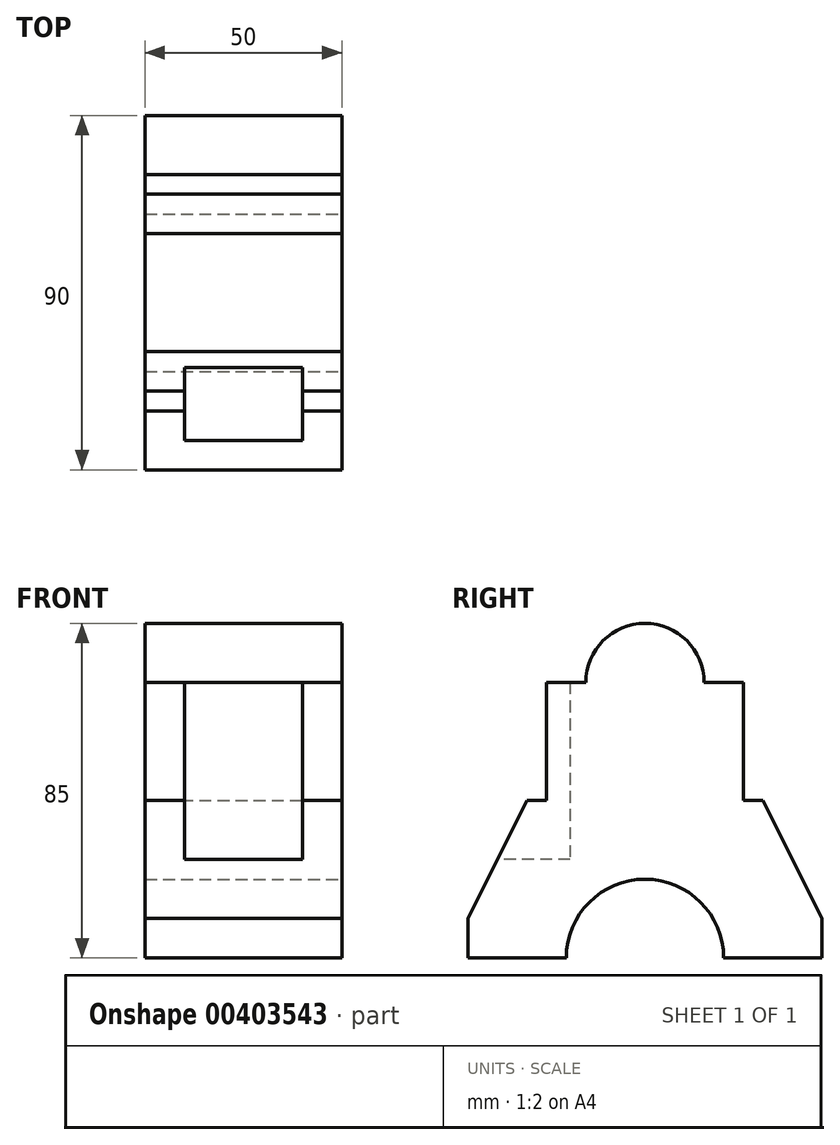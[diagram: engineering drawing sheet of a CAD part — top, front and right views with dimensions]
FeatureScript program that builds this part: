
annotation { "Feature Type Name" : "Feature", "Feature Type Description" : "" }
export const myFeature = defineFeature(function(context is Context, id is Id, definition is map)
    precondition{}
    {
        {
            var Q0;
            Q0=qCreatedBy(makeId("Right.planeOp"),FACE);
            var sketch = newSketch(context, id + "F0", { "sketchPlane" : qUnion([Q0])});
            skLineSegment(sketch, "E0", {"start": v(0, 0) * mm, "end": v(45, 0) * mm});
            skLineSegment(sketch, "E1", {"start": v(45, 0) * mm, "end": v(45, 10) * mm});
            skLineSegment(sketch, "E2", {"start": v(45, 10) * mm, "end": v(30, 40) * mm});
            skLineSegment(sketch, "E3", {"start": v(30, 40) * mm, "end": v(25, 40) * mm});
            skLineSegment(sketch, "E4", {"start": v(25, 40) * mm, "end": v(25, 70) * mm});
            skLineSegment(sketch, "E5", {"start": v(25, 70) * mm, "end": v(0, 70) * mm});
            skLineSegment(sketch, "E6", {"start": v(0, 70) * mm, "end": v(0, 0) * mm, "construction": true});
            skLineSegment(sketch, "E7.MirrorCS", {"start": v(-30, 40) * mm, "end": v(-25, 40) * mm});
            skLineSegment(sketch, "E8.MirrorCS", {"start": v(-25, 40) * mm, "end": v(-25, 70) * mm});
            skLineSegment(sketch, "E9.MirrorCS", {"start": v(0, 0) * mm, "end": v(-45, 0) * mm});
            skLineSegment(sketch, "E10.MirrorCS", {"start": v(-25, 70) * mm, "end": v(0, 70) * mm});
            skLineSegment(sketch, "E11.MirrorCS", {"start": v(-45, 10) * mm, "end": v(-30, 40) * mm});
            skLineSegment(sketch, "E12.MirrorCS", {"start": v(-45, 0) * mm, "end": v(-45, 10) * mm});
            skSolve(sketch);
        }
        {
            var Q0;
            Q0 = qSketchRegion(id + "F0", true);
            extrude(context, id + "F1", {"entities" : qUnion([Q0]), "endBound" : BoundingType.SYMMETRIC, "oppositeDirection" : true, "depth" : 50 * mm});
        }
        {
            var Q0;
            Q0=makeQuery(id+"F1.opExtrude","CAP_FACE",FACE,{"disambiguationData":[OSD([sQuery(id+"F0.wireOp",EDGE,"E0"),sQuery(id+"F0.wireOp",EDGE,"E1"),sQuery(id+"F0.wireOp",EDGE,"E2"),sQuery(id+"F0.wireOp",EDGE,"E3"),sQuery(id+"F0.wireOp",EDGE,"E4"),sQuery(id+"F0.wireOp",EDGE,"E5"),sQuery(id+"F0.wireOp",EDGE,"E7.MirrorCS"),sQuery(id+"F0.wireOp",EDGE,"E8.MirrorCS"),sQuery(id+"F0.wireOp",EDGE,"E9.MirrorCS"),sQuery(id+"F0.wireOp",EDGE,"E10.MirrorCS"),sQuery(id+"F0.wireOp",EDGE,"E11.MirrorCS"),sQuery(id+"F0.wireOp",EDGE,"E12.MirrorCS")])],"isStart":true});
            var sketch = newSketch(context, id + "F2", { "sketchPlane" : qUnion([Q0])});
            skCircle(sketch, "E13", {"center": v(0, 0) * mm, "radius": 20 * mm});
            skSolve(sketch);
        }
        {
            var Q0;
            Q0 = qSketchRegion(id + "F2", true);
            extrude(context, id + "F3", {"entities" : qUnion([Q0]), "operationType" : NewBodyOperationType.REMOVE, "endBound" : BoundingType.THROUGH_ALL, "oppositeDirection" : true, "depth" : 25 * mm});
        }
        {
            var Q0;
            Q0=makeQuery(id+"F1.opExtrude","CAP_FACE",FACE,{"disambiguationData":[OSD([sQuery(id+"F0.wireOp",EDGE,"E0"),sQuery(id+"F0.wireOp",EDGE,"E1"),sQuery(id+"F0.wireOp",EDGE,"E2"),sQuery(id+"F0.wireOp",EDGE,"E3"),sQuery(id+"F0.wireOp",EDGE,"E4"),sQuery(id+"F0.wireOp",EDGE,"E5"),sQuery(id+"F0.wireOp",EDGE,"E7.MirrorCS"),sQuery(id+"F0.wireOp",EDGE,"E8.MirrorCS"),sQuery(id+"F0.wireOp",EDGE,"E9.MirrorCS"),sQuery(id+"F0.wireOp",EDGE,"E10.MirrorCS"),sQuery(id+"F0.wireOp",EDGE,"E11.MirrorCS"),sQuery(id+"F0.wireOp",EDGE,"E12.MirrorCS")])],"isStart":true});
            var sketch = newSketch(context, id + "F4", { "sketchPlane" : qUnion([Q0])});
            skCircle(sketch, "E14", {"center": v(0, 70) * mm, "radius": 15 * mm});
            skSolve(sketch);
        }
        {
            var Q0;
            Q0 = qSketchRegion(id + "F4", true);
            extrude(context, id + "F5", {"entities" : qUnion([Q0]), "operationType" : NewBodyOperationType.ADD, "oppositeDirection" : true, "depth" : 50 * mm});
        }
        {
            var Q0;
            Q0=makeQuery(id+"F1.opExtrude","SWEPT_FACE",FACE,{"disambiguationData":[OSD([sQuery(id+"F0.wireOp",EDGE,"E12.MirrorCS")])]});
            var sketch = newSketch(context, id + "F6", { "sketchPlane" : qUnion([Q0])});
            skLineSegment(sketch, "E15.bottom", {"start": v(-15, 70) * mm, "end": v(15, 70) * mm});
            skLineSegment(sketch, "E15.top", {"start": v(-15, 25) * mm, "end": v(15, 25) * mm});
            skLineSegment(sketch, "E15.left", {"start": v(-15, 70) * mm, "end": v(-15, 25) * mm});
            skLineSegment(sketch, "E15.right", {"start": v(15, 70) * mm, "end": v(15, 25) * mm});
            skSolve(sketch);
        }
        {
            var Q0;
            Q0 = qSketchRegion(id + "F6", true);
            extrude(context, id + "F7", {"entities" : qUnion([Q0]), "operationType" : NewBodyOperationType.REMOVE, "oppositeDirection" : true, "depth" : 26 * mm});
        }
    });
